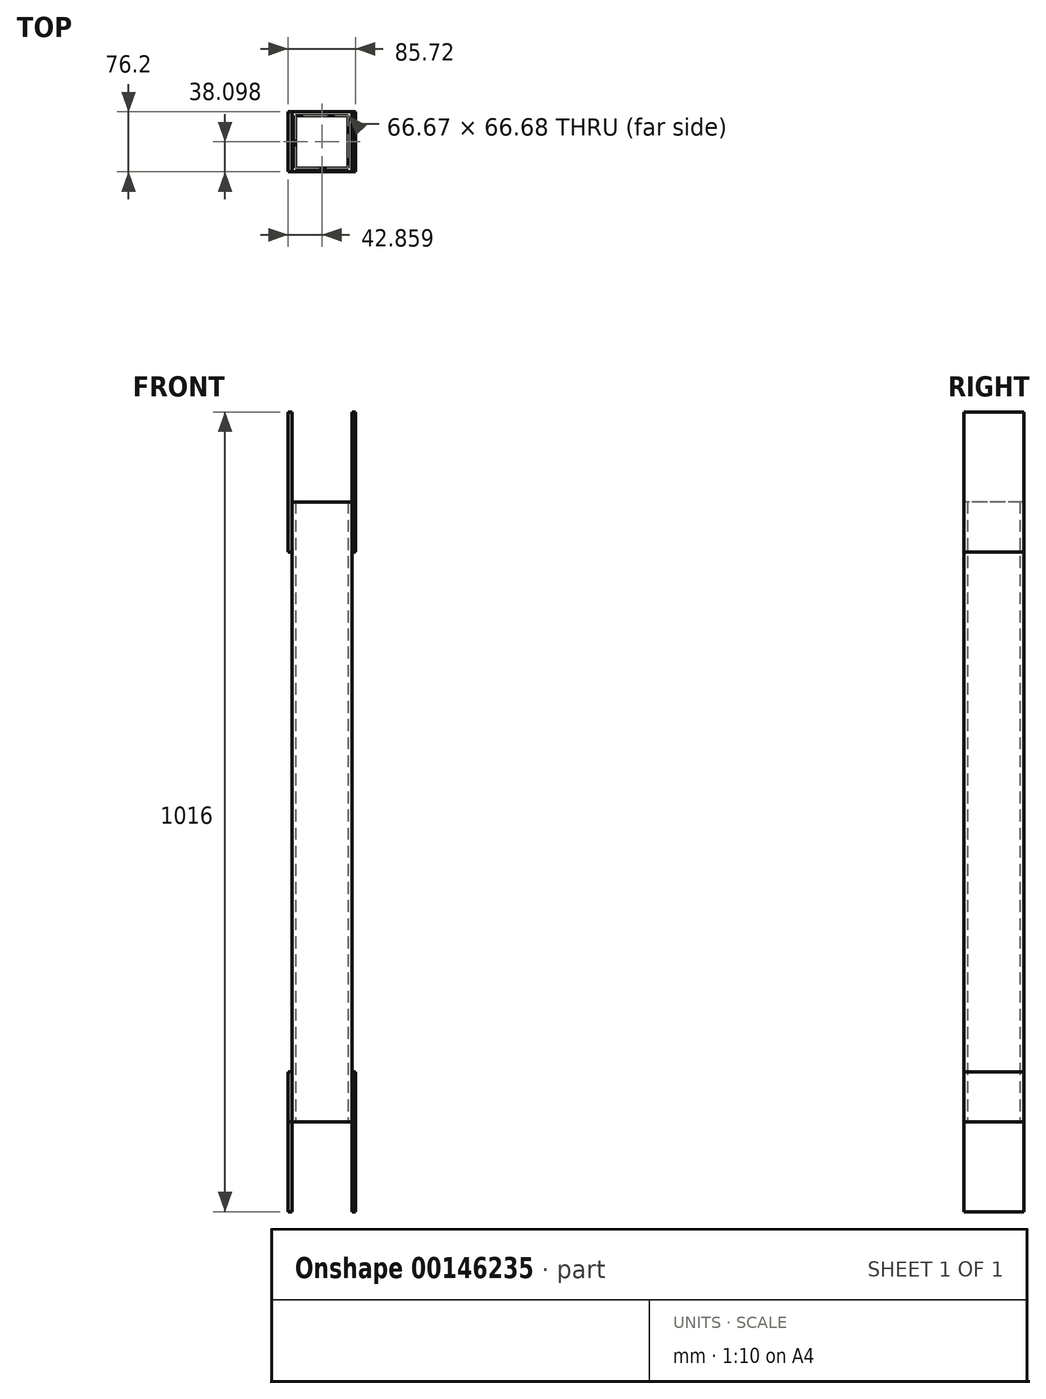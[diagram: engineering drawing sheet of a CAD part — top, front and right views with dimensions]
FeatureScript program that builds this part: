
annotation { "Feature Type Name" : "Feature", "Feature Type Description" : "" }
export const myFeature = defineFeature(function(context is Context, id is Id, definition is map)
    precondition{}
    {
        {
            var Q0;
            Q0=qCreatedBy(makeId("Top.planeOp"),FACE);
            var sketch = newSketch(context, id + "F0", { "sketchPlane" : qUnion([Q0])});
            skLineSegment(sketch, "E0.bottom", {"start": v(-65.26, 42.4) * mm, "end": v(10.94, 42.4) * mm});
            skLineSegment(sketch, "E0.top", {"start": v(-65.26, -33.8) * mm, "end": v(10.94, -33.8) * mm});
            skLineSegment(sketch, "E0.left", {"start": v(-65.26, 42.4) * mm, "end": v(-65.26, -33.8) * mm});
            skLineSegment(sketch, "E0.right", {"start": v(10.94, 42.4) * mm, "end": v(10.94, -33.8) * mm});
            skLineSegment(sketch, "E1.bottom", {"start": v(-60.5, 37.65) * mm, "end": v(6.18, 37.65) * mm});
            skLineSegment(sketch, "E1.top", {"start": v(-60.5, -29.03) * mm, "end": v(6.18, -29.03) * mm});
            skLineSegment(sketch, "E1.left", {"start": v(-60.5, 37.65) * mm, "end": v(-60.5, -29.03) * mm});
            skLineSegment(sketch, "E1.right", {"start": v(6.18, 37.65) * mm, "end": v(6.18, -29.03) * mm});
            skLineSegment(sketch, "E2.bottom", {"start": v(10.94, 42.4) * mm, "end": v(15.7, 42.4) * mm});
            skLineSegment(sketch, "E2.top", {"start": v(10.94, -33.8) * mm, "end": v(15.7, -33.8) * mm});
            skLineSegment(sketch, "E2.right", {"start": v(15.7, 42.4) * mm, "end": v(15.7, -33.8) * mm});
            skLineSegment(sketch, "E3.bottom", {"start": v(-65.26, 42.4) * mm, "end": v(-70.02, 42.4) * mm});
            skLineSegment(sketch, "E3.top", {"start": v(-65.26, -33.8) * mm, "end": v(-70.02, -33.8) * mm});
            skLineSegment(sketch, "E3.right", {"start": v(-70.02, 42.4) * mm, "end": v(-70.02, -33.8) * mm});
            skSolve(sketch);
        }
        {
            var Q0;
            Q0=makeQuery(id+"F0.imprint","IMPRINT",FACE,{"disambiguationData":[TD([[makeQuery(id+"F0.imprint","IMPRINT",EDGE,{"derivedFrom":sQuery(id+"F0.wireOp",EDGE,"E0.bottom")}),-1.0]])]});
            extrude(context, id + "F1", {"entities" : qUnion([Q0]), "depth" : 787.4 * mm});
        }
        {
            var Q0;
            Q0=makeQuery(id+"F0.imprint","IMPRINT",FACE,{"disambiguationData":[TD([[makeQuery(id+"F0.imprint","IMPRINT",EDGE,{"derivedFrom":sQuery(id+"F0.wireOp",EDGE,"E2.bottom")}),-1.0]])]});
            var Q1;
            Q1=makeQuery(id+"F0.imprint","IMPRINT",FACE,{"disambiguationData":[TD([[makeQuery(id+"F0.imprint","IMPRINT",EDGE,{"derivedFrom":sQuery(id+"F0.wireOp",EDGE,"E3.bottom")}),1.0]])]});
            extrude(context, id + "F3", {"entities" : qUnion([Q0, Q1]), "oppositeDirection" : true, "depth" : 114.3 * mm});
        }
        {
            var Q0;
            Q0=makeQuery(id+"F0.imprint","IMPRINT",FACE,{"disambiguationData":[TD([[makeQuery(id+"F0.imprint","IMPRINT",EDGE,{"derivedFrom":sQuery(id+"F0.wireOp",EDGE,"E2.bottom")}),-1.0]])]});
            var Q1;
            Q1=makeQuery(id+"F0.imprint","IMPRINT",FACE,{"disambiguationData":[TD([[makeQuery(id+"F0.imprint","IMPRINT",EDGE,{"derivedFrom":sQuery(id+"F0.wireOp",EDGE,"E3.bottom")}),1.0]])]});
            extrude(context, id + "F4", {"entities" : qUnion([Q0, Q1]), "depth" : 901.7 * mm});
        }
        {
            var Q0;
            Q0=makeQuery(id+"F0.imprint","IMPRINT",FACE,{"disambiguationData":[TD([[makeQuery(id+"F0.imprint","IMPRINT",EDGE,{"derivedFrom":sQuery(id+"F0.wireOp",EDGE,"E2.bottom")}),-1.0]])]});
            var Q1;
            Q1=makeQuery(id+"F0.imprint","IMPRINT",FACE,{"disambiguationData":[TD([[makeQuery(id+"F0.imprint","IMPRINT",EDGE,{"derivedFrom":sQuery(id+"F0.wireOp",EDGE,"E3.bottom")}),1.0]])]});
            extrude(context, id + "F2", {"entities" : qUnion([Q0, Q1]), "operationType" : NewBodyOperationType.REMOVE, "depth" : 723.9 * mm});
        }
        {
            var Q0;
            Q0=makeQuery(id+"F0.imprint","IMPRINT",FACE,{"disambiguationData":[TD([[makeQuery(id+"F0.imprint","IMPRINT",EDGE,{"derivedFrom":sQuery(id+"F0.wireOp",EDGE,"E2.bottom")}),-1.0]])]});
            var Q1;
            Q1=makeQuery(id+"F0.imprint","IMPRINT",FACE,{"disambiguationData":[TD([[makeQuery(id+"F0.imprint","IMPRINT",EDGE,{"derivedFrom":sQuery(id+"F0.wireOp",EDGE,"E3.bottom")}),1.0]])]});
            extrude(context, id + "F5", {"entities" : qUnion([Q0, Q1]), "depth" : 63.5 * mm});
        }
    });
